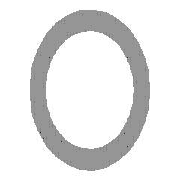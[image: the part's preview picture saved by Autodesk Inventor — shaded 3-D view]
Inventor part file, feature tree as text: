
AUTODESK INVENTOR PART (.ipt)
format: ipt  version: 2013 (Build 170138000, 138)  size: 108,032 bytes
history: native  units: mm (DEFAULTED — no unit token found)
features: other x3, sketch x3, plane x1
ambient origin geometry x8: Origin, YZ Plane, XZ Plane, XY Plane, X Axis, Y Axis, Z Axis, Center Point
bodies: Solid1 (feature_tree), Body (feature_tree)
feature tree (7):
  other  "Driven Length"
  other  "Start plane"
  other  "End plane"
  sketch  "Sketch1"  dims[d0=21.336mm]
  sketch  "Sketch2"  dims[d1=2.7686mm]
  plane  "Work Plane3"
  sketch  "Sketch3"  dims[d2=1524.0mm d3=0.0mm d5=-0.0mm d6=1524.0mm d7=90.0deg d8=1524.0mm]
